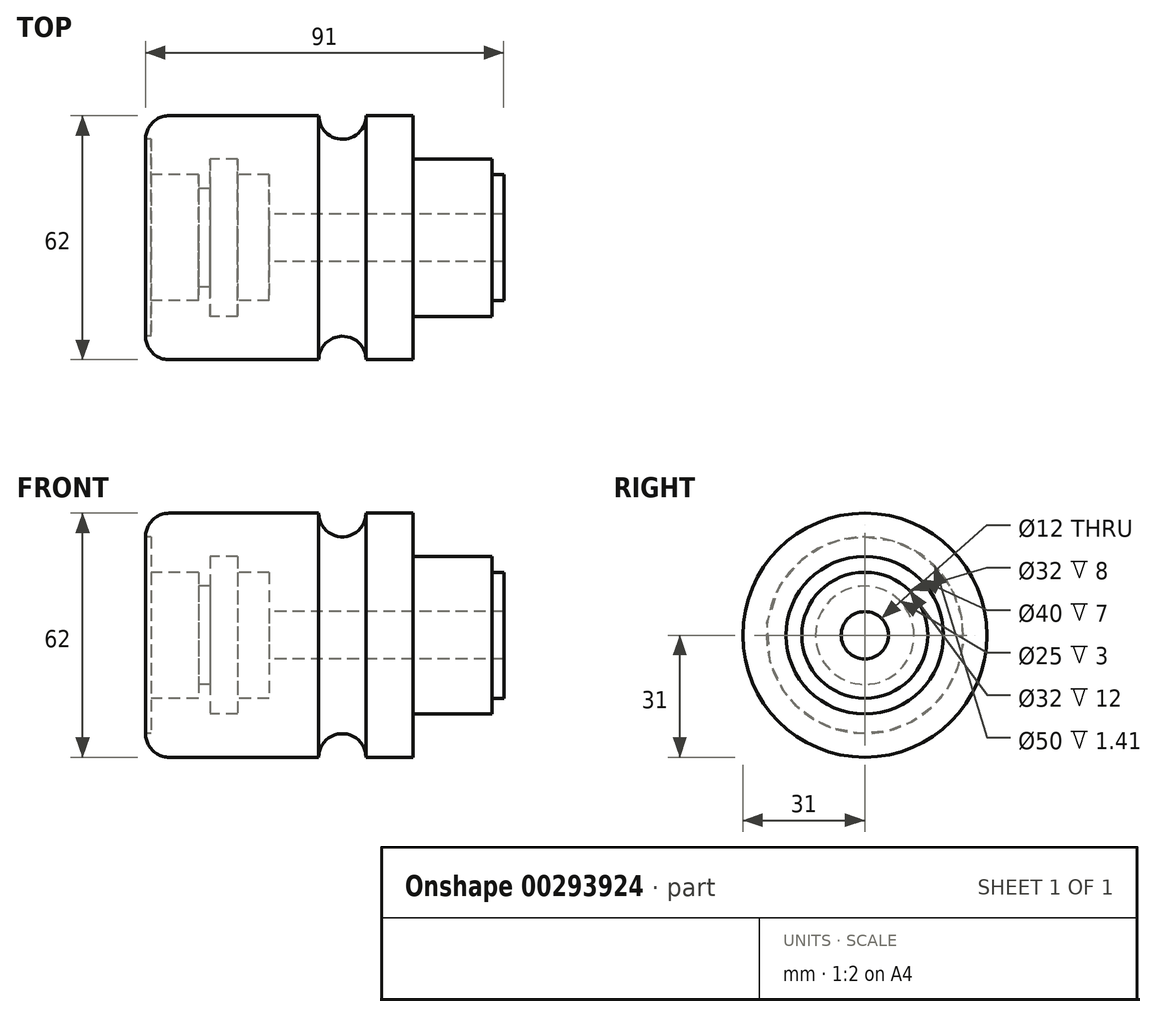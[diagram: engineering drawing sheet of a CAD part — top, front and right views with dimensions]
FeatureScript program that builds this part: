
annotation { "Feature Type Name" : "Feature", "Feature Type Description" : "" }
export const myFeature = defineFeature(function(context is Context, id is Id, definition is map)
    precondition{}
    {
        {
            var Q0;
            Q0=qCreatedBy(makeId("Front.planeOp"),FACE);
            var sketch = newSketch(context, id + "F0", { "sketchPlane" : qUnion([Q0])});
            skLineSegment(sketch, "E0", {"start": v(111.36, 0) * mm, "end": v(-48.64, 0) * mm, "construction": true});
            skLineSegment(sketch, "E1", {"start": v(0, 0) * mm, "end": v(-7.45, 0) * mm});
            skLineSegment(sketch, "E2", {"start": v(-7.45, 0) * mm, "end": v(-7.45, 31) * mm});
            skLineSegment(sketch, "E3", {"start": v(-7.45, 31) * mm, "end": v(36.55, 31) * mm});
            skLineSegment(sketch, "E4", {"start": v(60.55, 31) * mm, "end": v(60.55, 20) * mm});
            skLineSegment(sketch, "E5", {"start": v(60.55, 20) * mm, "end": v(80.55, 20) * mm});
            skLineSegment(sketch, "E6", {"start": v(80.55, 20) * mm, "end": v(80.55, 16) * mm});
            skLineSegment(sketch, "E7", {"start": v(80.55, 16) * mm, "end": v(83.55, 16) * mm});
            skLineSegment(sketch, "E8", {"start": v(83.55, 16) * mm, "end": v(83.55, 0) * mm});
            skLineSegment(sketch, "E9", {"start": v(75.8, 0) * mm, "end": v(111.36, 0) * mm, "construction": true});
            skArc(sketch, "E10", {"start": v(48.55, 31) * mm, "mid": v(42.55, 25) * mm, "end": v(36.55, 31) * mm});
            skLineSegment(sketch, "E11.trimOffspring", {"start": v(48.55, 31) * mm, "end": v(60.55, 31) * mm});
            skLineSegment(sketch, "E12", {"start": v(75.8, 0) * mm, "end": v(100.34, 0) * mm, "construction": true});
            skLineSegment(sketch, "E13", {"start": v(-7.45, 0) * mm, "end": v(83.55, 0) * mm});
            skSolve(sketch);
        }
        {
            var Q0;
            Q0 = qSketchRegion(id + "F0", true);
            var Q1;
            Q1=sQuery(id+"F0.wireOp",EDGE,"E13");
            revolve(context, id + "F1", {"entities" : qUnion([Q0]), "axis" : qUnion([Q1]), "revolveType" : RevolveType.FULL});
        }
        {
            var Q0;
            Q0=qCreatedBy(makeId("Front.planeOp"),FACE);
            var sketch = newSketch(context, id + "F2", { "sketchPlane" : qUnion([Q0])});
            skLineSegment(sketch, "E14", {"start": v(-15.85, 0) * mm, "end": v(100.03, 0) * mm, "construction": true});
            skLineSegment(sketch, "E15", {"start": v(-8.54, 0) * mm, "end": v(-8.54, 25) * mm});
            skLineSegment(sketch, "E16", {"start": v(-8.54, 25) * mm, "end": v(-6.04, 25) * mm});
            skLineSegment(sketch, "E17", {"start": v(-6.04, 25) * mm, "end": v(-6.04, 16) * mm});
            skLineSegment(sketch, "E18", {"start": v(-6.04, 16) * mm, "end": v(5.96, 16) * mm});
            skLineSegment(sketch, "E19", {"start": v(5.96, 16) * mm, "end": v(5.96, 12.5) * mm});
            skLineSegment(sketch, "E20", {"start": v(5.96, 12.5) * mm, "end": v(8.96, 12.5) * mm});
            skLineSegment(sketch, "E21", {"start": v(8.96, 12.5) * mm, "end": v(8.96, 20) * mm});
            skLineSegment(sketch, "E22", {"start": v(8.96, 20) * mm, "end": v(15.96, 20) * mm});
            skLineSegment(sketch, "E23", {"start": v(15.96, 20) * mm, "end": v(15.96, 16) * mm});
            skLineSegment(sketch, "E24", {"start": v(15.96, 16) * mm, "end": v(23.96, 16) * mm});
            skLineSegment(sketch, "E25", {"start": v(23.96, 16) * mm, "end": v(23.96, 6) * mm});
            skLineSegment(sketch, "E26", {"start": v(23.96, 6) * mm, "end": v(90.9, 6) * mm});
            skLineSegment(sketch, "E27", {"start": v(90.9, 6) * mm, "end": v(90.9, 0) * mm});
            skLineSegment(sketch, "E28", {"start": v(90.9, 0) * mm, "end": v(-8.54, 0) * mm});
            skSolve(sketch);
        }
        {
            var Q0;
            Q0 = qSketchRegion(id + "F2", true);
            var Q1;
            Q1=sQuery(id+"F2.wireOp",EDGE,"E28");
            revolve(context, id + "F3", {"operationType" : NewBodyOperationType.REMOVE, "entities" : qUnion([Q0]), "axis" : qUnion([Q1]), "revolveType" : RevolveType.FULL, "oppositeDirection" : true});
        }
        {
            var Q0;
            Q0=makeQuery(id+"F1.opRevolve","SWEPT_EDGE",EDGE,{"disambiguationData":[OSD([sQuery(id+"F0.wireOp",EDGE,"E2"),sQuery(id+"F0.wireOp",EDGE,"E3")])]});
            fillet(context, id + "F4", {"entities" : qUnion([Q0]), "radius" : 6 * mm, "tangentPropagation" : true, "allowEdgeOverflow" : false});
        }
    });
